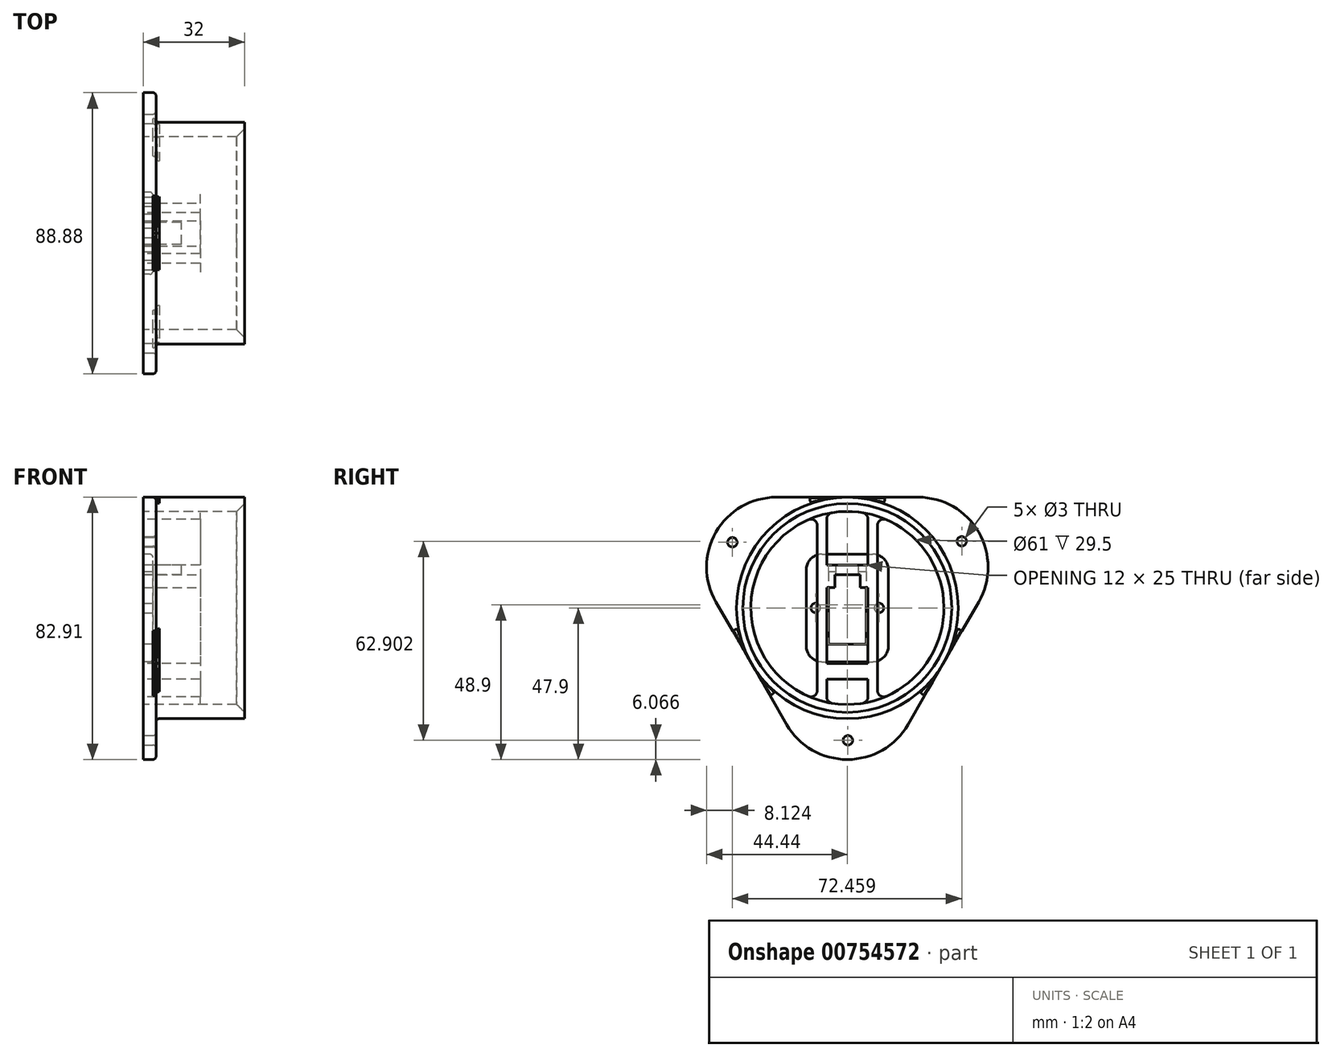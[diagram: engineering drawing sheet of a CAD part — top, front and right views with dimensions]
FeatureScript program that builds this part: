
annotation { "Feature Type Name" : "Feature", "Feature Type Description" : "" }
export const myFeature = defineFeature(function(context is Context, id is Id, definition is map)
    precondition{}
    {
        {
            var Q0;
            Q0=qCreatedBy(makeId("Right.planeOp"),FACE);
            var sketch = newSketch(context, id + "F0", { "sketchPlane" : qUnion([Q0])});
            skLineSegment(sketch, "E0.bottom", {"start": v(-6, 11.5) * mm, "end": v(6, 11.5) * mm});
            skLineSegment(sketch, "E0.top", {"start": v(-6, -11.5) * mm, "end": v(6, -11.5) * mm});
            skLineSegment(sketch, "E0.left", {"start": v(-6, 11.5) * mm, "end": v(-6, -11.5) * mm});
            skLineSegment(sketch, "E0.right", {"start": v(6, 11.5) * mm, "end": v(6, -11.5) * mm});
            skPoint(sketch, "E0.middle", {"position": v(0, 0) * mm});
            skLineSegment(sketch, "E1", {"start": v(0, 11.5) * mm, "end": v(-2.5, 11.5) * mm});
            skLineSegment(sketch, "E2", {"start": v(-2.5, 11.5) * mm, "end": v(-2.5, 13.5) * mm});
            skLineSegment(sketch, "E3", {"start": v(-2.5, 13.5) * mm, "end": v(2.5, 13.5) * mm});
            skLineSegment(sketch, "E4", {"start": v(2.5, 13.5) * mm, "end": v(2.5, 11.5) * mm});
            skLineSegment(sketch, "E5.bottom", {"start": v(-13, -17) * mm, "end": v(13, -17) * mm});
            skLineSegment(sketch, "E5.top", {"start": v(-13, 17) * mm, "end": v(13, 17) * mm});
            skLineSegment(sketch, "E5.left", {"start": v(-13, -17) * mm, "end": v(-13, 17) * mm});
            skLineSegment(sketch, "E5.right", {"start": v(13, -17) * mm, "end": v(13, 17) * mm});
            skSolve(sketch);
        }
        {
            var Q0;
            Q0=makeQuery(id+"F0.imprint","IMPRINT",FACE,{"disambiguationData":[TD([[makeQuery(id+"F0.imprint","IMPRINT",EDGE,{"derivedFrom":sQuery(id+"F0.wireOp",EDGE,"E0.top")}),-1.0]])]});
            extrude(context, id + "F1", {"entities" : qUnion([Q0]), "depth" : 3 * mm, "offsetDistance" : 25 * mm});
        }
        {
            var Q0;
            Q0=makeQuery(id+"F1.opExtrude","SWEPT_EDGE",EDGE,{"disambiguationData":[OSD([sQuery(id+"F0.wireOp",EDGE,"E5.top"),sQuery(id+"F0.wireOp",EDGE,"E5.left")])]});
            var Q1;
            Q1=makeQuery(id+"F1.opExtrude","SWEPT_EDGE",EDGE,{"disambiguationData":[OSD([sQuery(id+"F0.wireOp",EDGE,"E5.top"),sQuery(id+"F0.wireOp",EDGE,"E5.right")])]});
            var Q2;
            Q2=makeQuery(id+"F1.opExtrude","SWEPT_EDGE",EDGE,{"disambiguationData":[OSD([sQuery(id+"F0.wireOp",EDGE,"E5.bottom"),sQuery(id+"F0.wireOp",EDGE,"E5.right")])]});
            var Q3;
            Q3=makeQuery(id+"F1.opExtrude","SWEPT_EDGE",EDGE,{"disambiguationData":[OSD([sQuery(id+"F0.wireOp",EDGE,"E5.bottom"),sQuery(id+"F0.wireOp",EDGE,"E5.left")])]});
            fillet(context, id + "F2", {"entities" : qUnion([Q0, Q1, Q2, Q3]), "radius" : 5 * mm, "tangentPropagation" : true, "allowEdgeOverflow" : false});
        }
        {
            var Q0;
            {var subQ0=sQuery(id+"F0.wireOp",EDGE,"E5.left");var subQ1=sQuery(id+"F0.wireOp",EDGE,"E5.top");Q0=makeQuery(id+"F2.opFillet","BLEND_EDGE",EDGE,{"blendedFrom":[makeQuery(id+"F1.opExtrude","SWEPT_EDGE",EDGE,{"disambiguationData":[OSD([subQ1,subQ0])]}),makeQuery(id+"F1.opExtrude","CAP_FACE",FACE,{"disambiguationData":[OSD([sQuery(id+"F0.wireOp",EDGE,"E0.bottom"),sQuery(id+"F0.wireOp",EDGE,"E0.top"),sQuery(id+"F0.wireOp",EDGE,"E0.left"),sQuery(id+"F0.wireOp",EDGE,"E0.right"),sQuery(id+"F0.wireOp",EDGE,"E2"),sQuery(id+"F0.wireOp",EDGE,"E3"),sQuery(id+"F0.wireOp",EDGE,"E4"),sQuery(id+"F0.wireOp",EDGE,"E5.bottom"),subQ1,subQ0,sQuery(id+"F0.wireOp",EDGE,"E5.right")])],"isStart":false})],"blendedInto":[makeQuery(id+"F1.opExtrude","CAP_FACE",FACE,{"disambiguationData":[OSD([sQuery(id+"F0.wireOp",EDGE,"E0.bottom"),sQuery(id+"F0.wireOp",EDGE,"E0.top"),sQuery(id+"F0.wireOp",EDGE,"E0.left"),sQuery(id+"F0.wireOp",EDGE,"E0.right"),sQuery(id+"F0.wireOp",EDGE,"E2"),sQuery(id+"F0.wireOp",EDGE,"E3"),sQuery(id+"F0.wireOp",EDGE,"E4"),sQuery(id+"F0.wireOp",EDGE,"E5.bottom"),subQ1,subQ0,sQuery(id+"F0.wireOp",EDGE,"E5.right")])],"isStart":false})]});}
            fillet(context, id + "F3", {"entities" : qUnion([Q0]), "radius" : 1 * mm, "tangentPropagation" : true, "allowEdgeOverflow" : false});
        }
        {
            var Q0;
            Q0=makeQuery(id+"F1.opExtrude","CAP_FACE",FACE,{"disambiguationData":[OSD([sQuery(id+"F0.wireOp",EDGE,"E0.bottom"),sQuery(id+"F0.wireOp",EDGE,"E0.top"),sQuery(id+"F0.wireOp",EDGE,"E0.left"),sQuery(id+"F0.wireOp",EDGE,"E0.right"),sQuery(id+"F0.wireOp",EDGE,"E2"),sQuery(id+"F0.wireOp",EDGE,"E3"),sQuery(id+"F0.wireOp",EDGE,"E4"),sQuery(id+"F0.wireOp",EDGE,"E5.bottom"),sQuery(id+"F0.wireOp",EDGE,"E5.top"),sQuery(id+"F0.wireOp",EDGE,"E5.left"),sQuery(id+"F0.wireOp",EDGE,"E5.right")])],"isStart":false});
            var sketch = newSketch(context, id + "F4", { "sketchPlane" : qUnion([Q0])});
            skCircle(sketch, "E6", {"center": v(-10, 0) * mm, "radius": 1.5 * mm});
            skCircle(sketch, "E7", {"center": v(10, 0) * mm, "radius": 1.5 * mm});
            skPoint(sketch, "E8", {"position": v(-12, 0) * mm});
            skSolve(sketch);
        }
        {
            var Q0;
            Q0 = qSketchRegion(id + "F4", true);
            extrude(context, id + "F5", {"entities" : qUnion([Q0]), "operationType" : NewBodyOperationType.REMOVE, "oppositeDirection" : true, "depth" : 25 * mm, "offsetDistance" : 25 * mm});
        }
        {
            var Q0;
            Q0=qCreatedBy(makeId("Right.planeOp"),FACE);
            var sketch = newSketch(context, id + "F6", { "sketchPlane" : qUnion([Q0])});
            skCircle(sketch, "E9", {"center": v(0, 0) * mm, "radius": 35 * mm});
            skCircle(sketch, "E10", {"center": v(0, 0) * mm, "radius": 30.5 * mm});
            skLineSegment(sketch, "E11", {"start": v(-9.5, 28.98) * mm, "end": v(-9.5, -28.98) * mm});
            skLineSegment(sketch, "E12", {"start": v(9.5, 28.98) * mm, "end": v(9.5, -28.98) * mm});
            skLineSegment(sketch, "E13", {"start": v(-6.5, 29.8) * mm, "end": v(-6.5, -29.8) * mm});
            skLineSegment(sketch, "E14", {"start": v(6.5, 29.8) * mm, "end": v(6.5, -29.8) * mm});
            skLineSegment(sketch, "E15", {"start": v(0, 30.5) * mm, "end": v(0, 13.5) * mm});
            skLineSegment(sketch, "E16", {"start": v(0, 13.5) * mm, "end": v(6.5, 13.5) * mm});
            skLineSegment(sketch, "E17", {"start": v(6.5, 13.5) * mm, "end": v(-6.5, 13.5) * mm});
            skLineSegment(sketch, "E18", {"start": v(-6.5, 6.5) * mm, "end": v(6.5, 6.5) * mm});
            skLineSegment(sketch, "E19", {"start": v(-6.5, 6.5) * mm, "end": v(-6.5, -17.5) * mm});
            skLineSegment(sketch, "E20", {"start": v(-6.5, -17.5) * mm, "end": v(6.5, -17.5) * mm});
            skLineSegment(sketch, "E21", {"start": v(-6.5, -22.5) * mm, "end": v(6.5, -22.5) * mm});
            skSolve(sketch);
        }
        {
            var Q0;
            Q0 = qSketchRegion(id + "F6", true);
            var Q1;
            {var subQ4=sQuery(id+"F6.wireOp",EDGE,"E11");Q1=makeQuery(id+"F6.imprint","IMPRINT",FACE,{"disambiguationData":[TD([[makeQuery(id+"F6.imprint","IMPRINT",EDGE,{"derivedFrom":subQ4}),1.0]])]});}
            var Q2;
            {var subQ4=sQuery(id+"F6.wireOp",EDGE,"E18");Q2=makeQuery(id+"F6.imprint","IMPRINT",FACE,{"disambiguationData":[TD([[makeQuery(id+"F6.imprint","IMPRINT",EDGE,{"derivedFrom":subQ4}),1.0]])]});}
            var Q3;
            {var subQ0=sQuery(id+"F6.wireOp",EDGE,"E12");Q3=makeQuery(id+"F6.imprint","IMPRINT",FACE,{"disambiguationData":[TD([[makeQuery(id+"F6.imprint","IMPRINT",EDGE,{"derivedFrom":subQ0}),-1.0]])]});}
            var Q4;
            {var subQ0=sQuery(id+"F6.wireOp",EDGE,"E20");Q4=makeQuery(id+"F6.imprint","IMPRINT",FACE,{"disambiguationData":[TD([[makeQuery(id+"F6.imprint","IMPRINT",EDGE,{"derivedFrom":subQ0}),-1.0]])]});}
            extrude(context, id + "F7", {"entities" : qUnion([Q0, Q1, Q2, Q3, Q4]), "depth" : 18 * mm, "offsetDistance" : 25 * mm});
        }
        {
            var Q0;
            Q0=makeQuery(id+"F7.opExtrude","CAP_FACE",FACE,{"disambiguationData":[OSD([sQuery(id+"F6.wireOp",EDGE,"E9"),sQuery(id+"F6.wireOp",EDGE,"E10"),sQuery(id+"F6.wireOp",EDGE,"E11"),sQuery(id+"F6.wireOp",EDGE,"E12"),sQuery(id+"F6.wireOp",EDGE,"E13"),sQuery(id+"F6.wireOp",EDGE,"E14"),sQuery(id+"F6.wireOp",EDGE,"E17"),sQuery(id+"F6.wireOp",EDGE,"E18"),sQuery(id+"F6.wireOp",EDGE,"E19"),sQuery(id+"F6.wireOp",EDGE,"E20"),sQuery(id+"F6.wireOp",EDGE,"E21")])],"isStart":true});
            var sketch = newSketch(context, id + "F8", { "sketchPlane" : qUnion([Q0])});
            skLineSegment(sketch, "E22.bottom", {"start": v(3.5, 6.5) * mm, "end": v(-3.5, 6.5) * mm});
            skLineSegment(sketch, "E22.top", {"start": v(3.5, 13.5) * mm, "end": v(-3.5, 13.5) * mm});
            skLineSegment(sketch, "E22.left", {"start": v(3.5, 6.5) * mm, "end": v(3.5, 13.5) * mm});
            skLineSegment(sketch, "E22.right", {"start": v(-3.5, 6.5) * mm, "end": v(-3.5, 13.5) * mm});
            skSolve(sketch);
        }
        {
            var Q0;
            Q0 = qSketchRegion(id + "F8", true);
            extrude(context, id + "F9", {"entities" : qUnion([Q0]), "operationType" : NewBodyOperationType.REMOVE, "oppositeDirection" : true, "depth" : 12 * mm, "offsetDistance" : 25 * mm});
        }
        {
            var Q0;
            Q0=makeQuery(id+"F7.opExtrude","CAP_FACE",FACE,{"disambiguationData":[OSD([sQuery(id+"F6.wireOp",EDGE,"E9"),sQuery(id+"F6.wireOp",EDGE,"E10"),sQuery(id+"F6.wireOp",EDGE,"E11"),sQuery(id+"F6.wireOp",EDGE,"E12"),sQuery(id+"F6.wireOp",EDGE,"E13"),sQuery(id+"F6.wireOp",EDGE,"E14"),sQuery(id+"F6.wireOp",EDGE,"E17"),sQuery(id+"F6.wireOp",EDGE,"E18"),sQuery(id+"F6.wireOp",EDGE,"E19"),sQuery(id+"F6.wireOp",EDGE,"E20"),sQuery(id+"F6.wireOp",EDGE,"E21")])],"isStart":false});
            var sketch = newSketch(context, id + "F10", { "sketchPlane" : qUnion([Q0])});
            skLineSegment(sketch, "E23.bottom", {"start": v(4, 10.5) * mm, "end": v(-4, 10.5) * mm});
            skLineSegment(sketch, "E23.top", {"start": v(4, 2.5) * mm, "end": v(-4, 2.5) * mm});
            skLineSegment(sketch, "E23.left", {"start": v(4, 10.5) * mm, "end": v(4, 2.5) * mm});
            skLineSegment(sketch, "E23.right", {"start": v(-4, 10.5) * mm, "end": v(-4, 2.5) * mm});
            skPoint(sketch, "E23.middle", {"position": v(0, 6.5) * mm});
            skSolve(sketch);
        }
        {
            var Q0;
            Q0 = qSketchRegion(id + "F10", true);
            extrude(context, id + "F11", {"entities" : qUnion([Q0]), "operationType" : NewBodyOperationType.REMOVE, "oppositeDirection" : true, "depth" : 25 * mm, "offsetDistance" : 25 * mm});
        }
        {
            var Q0;
            Q0=makeQuery(id+"F7.opExtrude","CAP_FACE",FACE,{"disambiguationData":[OSD([sQuery(id+"F6.wireOp",EDGE,"E9"),sQuery(id+"F6.wireOp",EDGE,"E10"),sQuery(id+"F6.wireOp",EDGE,"E11"),sQuery(id+"F6.wireOp",EDGE,"E12"),sQuery(id+"F6.wireOp",EDGE,"E13"),sQuery(id+"F6.wireOp",EDGE,"E14"),sQuery(id+"F6.wireOp",EDGE,"E17"),sQuery(id+"F6.wireOp",EDGE,"E18"),sQuery(id+"F6.wireOp",EDGE,"E19"),sQuery(id+"F6.wireOp",EDGE,"E20"),sQuery(id+"F6.wireOp",EDGE,"E21")])],"isStart":false});
            var sketch = newSketch(context, id + "F12", { "sketchPlane" : qUnion([Q0])});
            skCircle(sketch, "E24", {"center": v(0, 0) * mm, "radius": 35 * mm});
            skCircle(sketch, "E25", {"center": v(0, 0) * mm, "radius": 30.5 * mm});
            skSolve(sketch);
        }
        {
            var Q0;
            Q0 = qSketchRegion(id + "F12", true);
            extrude(context, id + "F13", {"entities" : qUnion([Q0]), "operationType" : NewBodyOperationType.ADD, "depth" : 14 * mm, "offsetDistance" : 25 * mm});
        }
        {
            var Q0;
            {var subQ0=sQuery(id+"F6.wireOp",EDGE,"E11");var subQ1=sQuery(id+"F6.wireOp",EDGE,"E10");Q0=makeQuery(id+"F7.opExtrude","SWEPT_EDGE",EDGE,{"disambiguationData":[OSD([subQ1,subQ0]),TDD([makeQuery(id+"F6.imprint","INTERSECT",VERTEX,{"disambiguationData":[OD(0.0)],"derivedFrom":[subQ1,subQ0]})])]});}
            var Q1;
            {var subQ0=sQuery(id+"F6.wireOp",EDGE,"E13");var subQ1=sQuery(id+"F6.wireOp",EDGE,"E10");Q1=makeQuery(id+"F7.opExtrude","SWEPT_EDGE",EDGE,{"disambiguationData":[OSD([subQ1,subQ0]),TDD([makeQuery(id+"F6.imprint","INTERSECT",VERTEX,{"disambiguationData":[OD(0.0)],"derivedFrom":[subQ1,subQ0]})])]});}
            var Q2;
            {var subQ0=sQuery(id+"F6.wireOp",EDGE,"E14");var subQ1=sQuery(id+"F6.wireOp",EDGE,"E10");Q2=makeQuery(id+"F7.opExtrude","SWEPT_EDGE",EDGE,{"disambiguationData":[OSD([subQ1,subQ0]),TDD([makeQuery(id+"F6.imprint","INTERSECT",VERTEX,{"disambiguationData":[OD(0.0)],"derivedFrom":[subQ1,subQ0]})])]});}
            var Q3;
            {var subQ0=sQuery(id+"F6.wireOp",EDGE,"E12");var subQ1=sQuery(id+"F6.wireOp",EDGE,"E10");Q3=makeQuery(id+"F7.opExtrude","SWEPT_EDGE",EDGE,{"disambiguationData":[OSD([subQ1,subQ0]),TDD([makeQuery(id+"F6.imprint","INTERSECT",VERTEX,{"disambiguationData":[OD(0.0)],"derivedFrom":[subQ1,subQ0]})])]});}
            var Q4;
            {var subQ0=sQuery(id+"F6.wireOp",EDGE,"E11");var subQ1=sQuery(id+"F6.wireOp",EDGE,"E10");Q4=makeQuery(id+"F7.opExtrude","SWEPT_EDGE",EDGE,{"disambiguationData":[OSD([subQ1,subQ0]),TDD([makeQuery(id+"F6.imprint","INTERSECT",VERTEX,{"disambiguationData":[OD(1.0)],"derivedFrom":[subQ1,subQ0]})])]});}
            var Q5;
            {var subQ0=sQuery(id+"F6.wireOp",EDGE,"E13");var subQ1=sQuery(id+"F6.wireOp",EDGE,"E10");Q5=makeQuery(id+"F7.opExtrude","SWEPT_EDGE",EDGE,{"disambiguationData":[OSD([subQ1,subQ0]),TDD([makeQuery(id+"F6.imprint","INTERSECT",VERTEX,{"disambiguationData":[OD(1.0)],"derivedFrom":[subQ1,subQ0]})])]});}
            var Q6;
            {var subQ0=sQuery(id+"F6.wireOp",EDGE,"E14");var subQ1=sQuery(id+"F6.wireOp",EDGE,"E10");Q6=makeQuery(id+"F7.opExtrude","SWEPT_EDGE",EDGE,{"disambiguationData":[OSD([subQ1,subQ0]),TDD([makeQuery(id+"F6.imprint","INTERSECT",VERTEX,{"disambiguationData":[OD(1.0)],"derivedFrom":[subQ1,subQ0]})])]});}
            var Q7;
            {var subQ0=sQuery(id+"F6.wireOp",EDGE,"E12");var subQ1=sQuery(id+"F6.wireOp",EDGE,"E10");Q7=makeQuery(id+"F7.opExtrude","SWEPT_EDGE",EDGE,{"disambiguationData":[OSD([subQ1,subQ0]),TDD([makeQuery(id+"F6.imprint","INTERSECT",VERTEX,{"disambiguationData":[OD(1.0)],"derivedFrom":[subQ1,subQ0]})])]});}
            fillet(context, id + "F14", {"entities" : qUnion([Q0, Q1, Q2, Q3, Q4, Q5, Q6, Q7]), "radius" : 2 * mm, "tangentPropagation" : true, "allowEdgeOverflow" : false});
        }
        {
            var Q0;
            Q0=qCreatedBy(makeId("Right.planeOp"),FACE);
            var sketch = newSketch(context, id + "F15", { "sketchPlane" : qUnion([Q0])});
            skCircle(sketch, "E26", {"center": v(0, 0) * mm, "radius": 30.5 * mm});
            skCircle(sketch, "E27", {"center": v(0, 0) * mm, "radius": 35 * mm});
            skCircle(sketch, "E28.cCircle", {"center": v(0, 0) * mm, "radius": 35 * mm, "construction": true});
            skLineSegment(sketch, "E28.0", {"start": v(-60.62, 35) * mm, "end": v(60.62, 35) * mm});
            skLineSegment(sketch, "E28.1", {"start": v(60.62, 35) * mm, "end": v(0, -70) * mm});
            skLineSegment(sketch, "E28.2", {"start": v(0, -70) * mm, "end": v(-60.62, 35) * mm});
            skPoint(sketch, "E28.0.midPoint", {"position": v(0, 35) * mm});
            skSolve(sketch);
        }
        {
            var Q0;
            Q0 = qSketchRegion(id + "F15", true);
            extrude(context, id + "F16", {"entities" : qUnion([Q0]), "operationType" : NewBodyOperationType.ADD, "depth" : 4 * mm, "offsetDistance" : 25 * mm});
        }
        {
            var Q0;
            Q0=makeQuery(id+"F16.opExtrude","SWEPT_EDGE",EDGE,{"disambiguationData":[OSD([sQuery(id+"F15.wireOp",EDGE,"E28.1"),sQuery(id+"F15.wireOp",EDGE,"E28.2")])]});
            var Q1;
            Q1=makeQuery(id+"F16.opExtrude","SWEPT_EDGE",EDGE,{"disambiguationData":[OSD([sQuery(id+"F15.wireOp",EDGE,"E28.0"),sQuery(id+"F15.wireOp",EDGE,"E28.1")])]});
            var Q2;
            Q2=makeQuery(id+"F16.opExtrude","SWEPT_EDGE",EDGE,{"disambiguationData":[OSD([sQuery(id+"F15.wireOp",EDGE,"E28.0"),sQuery(id+"F15.wireOp",EDGE,"E28.2")])]});
            fillet(context, id + "F17", {"entities" : qUnion([Q0, Q1, Q2]), "radius" : 22.1 * mm, "tangentPropagation" : true, "allowEdgeOverflow" : false});
        }
        {
            var Q0;
            {var subQ0=sQuery(id+"F15.wireOp",EDGE,"E28.0");var subQ1=sQuery(id+"F15.wireOp",EDGE,"E28.2");var subQ2=makeQuery(id+"F16.opExtrude","CAP_FACE",FACE,{"disambiguationData":[OSD([sQuery(id+"F15.wireOp",EDGE,"E26"),subQ0,sQuery(id+"F15.wireOp",EDGE,"E28.1"),subQ1])],"isStart":false});Q0=makeQuery(id+"F16.boolean.opBoolean","SPLIT",FACE,{"disambiguationData":[TD([makeQuery(id+"F7.opExtrude","SWEPT_FACE",FACE,{"disambiguationData":[OSD([sQuery(id+"F6.wireOp",EDGE,"E9")])]}),makeQuery(id+"F13.opExtrude","SWEPT_FACE",FACE,{"disambiguationData":[OSD([sQuery(id+"F12.wireOp",EDGE,"E24")])]}),subQ2,makeQuery(id+"F16.opExtrude","SWEPT_FACE",FACE,{"disambiguationData":[OSD([subQ0])]}),makeQuery(id+"F16.opExtrude","SWEPT_FACE",FACE,{"disambiguationData":[OSD([subQ1])]})])],"derivedFrom":subQ2});}
            var sketch = newSketch(context, id + "F18", { "sketchPlane" : qUnion([Q0])});
            skCircle(sketch, "E29", {"center": v(-36.32, 20.77) * mm, "radius": 1.5 * mm});
            skCircle(sketch, "E30.1.0", {"center": v(0.17, -41.83) * mm, "radius": 1.5 * mm});
            skCircle(sketch, "E30.2.0", {"center": v(36.14, 21.07) * mm, "radius": 1.5 * mm});
            skPoint(sketch, "E30.center", {"position": v(0, 0) * mm});
            skSolve(sketch);
        }
        {
            var Q0;
            Q0 = qSketchRegion(id + "F18", true);
            extrude(context, id + "F19", {"entities" : qUnion([Q0]), "operationType" : NewBodyOperationType.REMOVE, "oppositeDirection" : true, "depth" : 25 * mm, "offsetDistance" : 25 * mm});
        }
        {
            var Q0;
            {var subQ0=sQuery(id+"F15.wireOp",EDGE,"E28.0");var subQ1=sQuery(id+"F15.wireOp",EDGE,"E28.2");var subQ2=makeQuery(id+"F16.opExtrude","CAP_FACE",FACE,{"disambiguationData":[OSD([sQuery(id+"F15.wireOp",EDGE,"E26"),subQ0,sQuery(id+"F15.wireOp",EDGE,"E28.1"),subQ1])],"isStart":false});Q0=makeQuery(id+"F16.boolean.opBoolean","SPLIT",FACE,{"disambiguationData":[TD([makeQuery(id+"F7.opExtrude","SWEPT_FACE",FACE,{"disambiguationData":[OSD([sQuery(id+"F6.wireOp",EDGE,"E9")])]}),makeQuery(id+"F13.opExtrude","SWEPT_FACE",FACE,{"disambiguationData":[OSD([sQuery(id+"F12.wireOp",EDGE,"E24")])]}),subQ2,makeQuery(id+"F16.opExtrude","SWEPT_FACE",FACE,{"disambiguationData":[OSD([subQ0])]}),makeQuery(id+"F16.opExtrude","SWEPT_FACE",FACE,{"disambiguationData":[OSD([subQ1])]})])],"derivedFrom":subQ2});}
            var Q1;
            {var subQ0=sQuery(id+"F15.wireOp",EDGE,"E28.2");var subQ1=sQuery(id+"F15.wireOp",EDGE,"E28.1");var subQ2=makeQuery(id+"F16.opExtrude","CAP_FACE",FACE,{"disambiguationData":[OSD([sQuery(id+"F15.wireOp",EDGE,"E26"),sQuery(id+"F15.wireOp",EDGE,"E28.0"),subQ1,subQ0])],"isStart":false});Q1=makeQuery(id+"F16.boolean.opBoolean","SPLIT",FACE,{"disambiguationData":[TD([makeQuery(id+"F7.opExtrude","SWEPT_FACE",FACE,{"disambiguationData":[OSD([sQuery(id+"F6.wireOp",EDGE,"E9")])]}),makeQuery(id+"F13.opExtrude","SWEPT_FACE",FACE,{"disambiguationData":[OSD([sQuery(id+"F12.wireOp",EDGE,"E24")])]}),subQ2,makeQuery(id+"F16.opExtrude","SWEPT_FACE",FACE,{"disambiguationData":[OSD([subQ1])]}),makeQuery(id+"F16.opExtrude","SWEPT_FACE",FACE,{"disambiguationData":[OSD([subQ0])]})])],"derivedFrom":subQ2});}
            var Q2;
            {var subQ0=sQuery(id+"F15.wireOp",EDGE,"E28.0");var subQ1=sQuery(id+"F15.wireOp",EDGE,"E28.1");var subQ2=makeQuery(id+"F16.opExtrude","CAP_FACE",FACE,{"disambiguationData":[OSD([sQuery(id+"F15.wireOp",EDGE,"E26"),subQ0,subQ1,sQuery(id+"F15.wireOp",EDGE,"E28.2")])],"isStart":false});Q2=makeQuery(id+"F16.boolean.opBoolean","SPLIT",FACE,{"disambiguationData":[TD([makeQuery(id+"F7.opExtrude","SWEPT_FACE",FACE,{"disambiguationData":[OSD([sQuery(id+"F6.wireOp",EDGE,"E9")])]}),makeQuery(id+"F13.opExtrude","SWEPT_FACE",FACE,{"disambiguationData":[OSD([sQuery(id+"F12.wireOp",EDGE,"E24")])]}),subQ2,makeQuery(id+"F16.opExtrude","SWEPT_FACE",FACE,{"disambiguationData":[OSD([subQ0])]}),makeQuery(id+"F16.opExtrude","SWEPT_FACE",FACE,{"disambiguationData":[OSD([subQ1])]})])],"derivedFrom":subQ2});}
            fillet(context, id + "F20", {"entities" : qUnion([Q0, Q1, Q2]), "radius" : 1 * mm, "tangentPropagation" : true, "allowEdgeOverflow" : false});
        }
        {
            var Q0;
            Q0=makeQuery(id+"F13.opExtrude","CAP_EDGE",EDGE,{"disambiguationData":[OSD([sQuery(id+"F12.wireOp",EDGE,"E25")])],"isStart":false});
            chamfer(context, id + "F21", {"entities" : qUnion([Q0]), "width" : 2.5 * mm, "tangentPropagation" : true});
        }
    });
